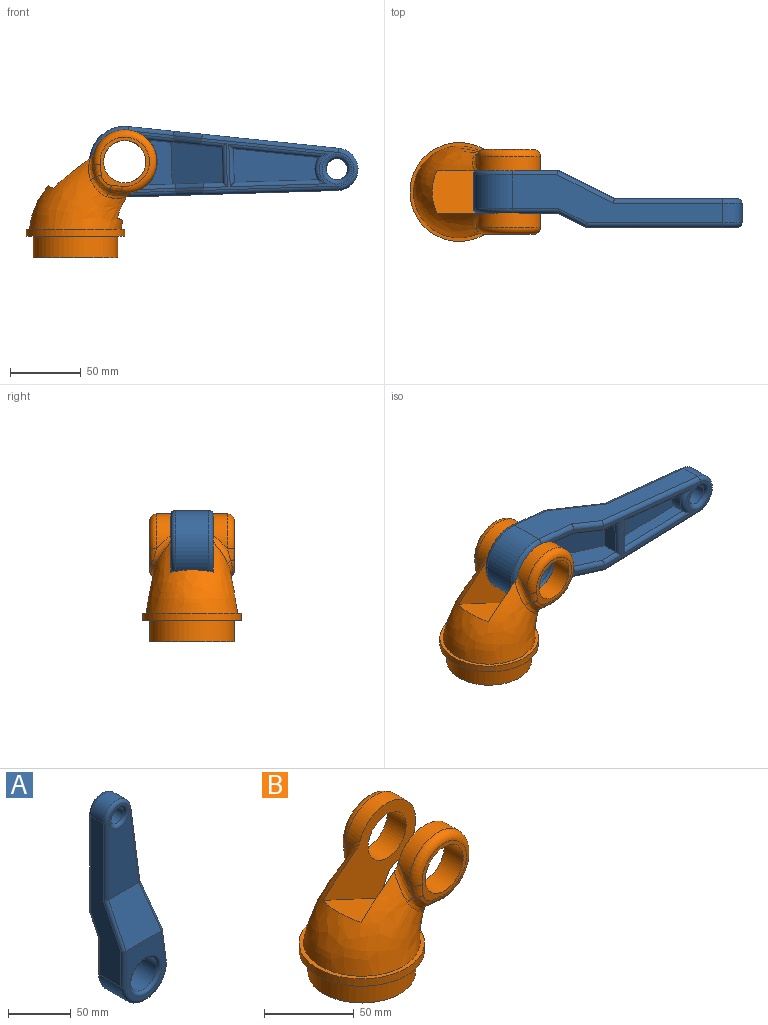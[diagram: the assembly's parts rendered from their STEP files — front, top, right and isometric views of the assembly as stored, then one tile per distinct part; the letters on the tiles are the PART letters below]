
ASSEMBLY  parts=2 mates=1
PART A: 56 faces, bbox 54.1x40x193.3 mm
  f0: plane 60.11x9mm, normal (-0.99,0,-0.13), area 545.8mm2, adj f19,f21,f22,f40
  f1: plane 53.62x29mm, normal (1,0,0), area 928.8mm2, adj f2,f16,f20,f23,f44,f45,f47
  f2: plane 36x29.72mm, normal (0,0.89,-0.45), area 1099.1mm2, adj f1,f16,f17,f23
  f3: plane 107.01x36.83mm, normal (0,1,0), area 546mm2, adj f5,f6,f24,f25,f27,f29,f40,f41
  f4: plane 57.02x44.01mm, normal (0,1,0), area 511.3mm2, adj f5,f6,f28,f29,f30,f31,f44,f46
  f5: plane 20.02x10.01mm, normal (0,0.89,-0.45), area 45.1mm2, adj f3,f4,f29,f48,f50,f51
  f6: plane 20x10mm, normal (0,0.89,-0.45), area 44.7mm2, adj f3,f4,f26,f45
  f7: plane 57x44mm, normal (0,-1,0), area 1207mm2, adj f13,f36,f38,f39,f53
  f8: cylinder r=25mm len=50mm, axis (0,1,0), area 1964.8mm2, adj f9,f11,f30,f38
  f9: plane 148.67x34mm, normal (0.99,0,0.13), area 2704.9mm2, adj f8,f10,f27,f29,f31,f35,f37,f39
  f10: cylinder r=15mm len=29.87mm, axis (0,1,0), area 631.8mm2, adj f9,f11,f25,f33
  f11: plane 150x34mm, normal (-1,0,0), area 2728.8mm2, adj f8,f10,f24,f26,f28,f32,f34,f36
  f12: plane 87x34.15mm, normal (0,-1,0), area 2064.6mm2, adj f13,f32,f33,f35,f52
  f13: plane 40.02x39.69mm, normal (0,-0.89,0.45), area 1655.1mm2, adj f7,f12,f34,f35,f37,f39
  f14: cylinder r=15mm len=30mm, axis (0,1,0), area 2261.9mm2, adj f53,f54
  f15: cylinder r=7.5mm len=15mm, axis (0,1,0), area 659.7mm2, adj f52,f55
  f16: plane 31.79x17.62mm, normal (0,1,0), area 369.9mm2, adj f1,f2,f17,f20
  f17: plane 51.5x29mm, normal (-0.99,0,-0.13), area 900.5mm2, adj f2,f16,f20,f23,f48,f50,f51
  f18: plane 59.06x9mm, normal (1,0,0), area 531.5mm2, adj f19,f21,f22,f43
  f19: plane 60.11x23.82mm, normal (0,1,0), area 1158.7mm2, adj f0,f18,f21,f22
  f20: cylinder r=23mm len=31.79mm, axis (0,1,0), area 668.8mm2, adj f1,f16,f17,f46
  f21: cylinder r=15.5mm len=15.77mm, axis (0,1,0), area 149.3mm2, adj f0,f18,f19,f42
  f22: plane 23.82x9mm, normal (0,0,1), area 214.4mm2, adj f0,f18,f19,f41
  f23: plane 24.9x11mm, normal (0,0,-1), area 273.9mm2, adj f1,f2,f17,f49
  f24: cylinder r=3mm len=95mm, axis (0,0,-1), area 446.5mm2, adj f3,f11,f25,f26
  f25: torus R=12mm, axis (0,-1,0), area 197.2mm2, adj f3,f10,f24,f27
  f26: cylinder r=3mm len=21.98mm, axis (0,-0.45,-0.89), area 105.4mm2, adj f6,f11,f24,f28
  f27: cylinder r=3mm len=96.98mm, axis (-0.13,0,0.99), area 458mm2, adj f3,f9,f25,f29
  f28: cylinder r=3mm len=35.71mm, axis (0,0,-1), area 166.1mm2, adj f4,f11,f26,f30
  f29: cylinder r=3mm len=22.37mm, axis (-0.12,0.44,0.89), area 110.1mm2, adj f3,f4,f5,f9,f27,f31
  f30: torus R=22mm, axis (0,-1,0), area 369mm2, adj f4,f8,f28,f31
  f31: cylinder r=3mm len=33.19mm, axis (-0.13,0,0.99), area 153.8mm2, adj f4,f9,f29,f30
  f32: cylinder r=3mm len=75.71mm, axis (0,0,1), area 354.6mm2, adj f11,f12,f33,f34
  f33: torus R=12mm, axis (0,1,0), area 197.2mm2, adj f10,f12,f32,f35
  f34: cylinder r=3mm len=41.98mm, axis (0,0.45,0.89), area 210.7mm2, adj f11,f13,f32,f36
  f35: cylinder r=3mm len=77.7mm, axis (0.13,0,-0.99), area 365.4mm2, adj f9,f12,f13,f33,f37
  f36: cylinder r=3mm len=35mm, axis (0,0,1), area 163.7mm2, adj f7,f11,f34,f38
  f37: cylinder r=3mm len=41.6mm, axis (0.12,-0.44,-0.89), area 204.2mm2, adj f9,f13,f35,f39
  f38: torus R=22mm, axis (0,-1,0), area 369mm2, adj f7,f8,f36,f39
  f39: cylinder r=3mm len=32.48mm, axis (0.13,0,-0.99), area 151.3mm2, adj f7,f9,f13,f37,f38
  f40: cylinder r=3mm len=70.18mm, axis (0.13,0,-0.99), area 301.3mm2, adj f0,f3,f41,f42
  f41: cylinder r=3mm len=30.25mm, axis (-1,0,0), area 123.3mm2, adj f3,f22,f40,f43
  f42: torus R=12.5mm, axis (0,-1,0), area 90.8mm2, adj f3,f21,f40,f43
  f43: cylinder r=3mm len=68.39mm, axis (0,0,1), area 293.1mm2, adj f3,f18,f41,f42
  f44: cylinder r=3mm len=35.71mm, axis (0,0,1), area 110.5mm2, adj f1,f4,f45,f46
  f45: cylinder r=3mm len=21.98mm, axis (0,0.45,0.89), area 105.4mm2, adj f1,f6,f44,f47
  f46: torus R=20mm, axis (0,-1,0), area 191.3mm2, adj f4,f20,f44,f48
  f47: cylinder r=3mm len=17.11mm, axis (0,0,1), area 70.4mm2, adj f1,f3,f45,f49
  f48: cylinder r=3mm len=33.45mm, axis (0.13,0,-0.99), area 99.4mm2, adj f4,f5,f17,f46,f50
  f49: cylinder r=3mm len=30.52mm, axis (1,0,0), area 127mm2, adj f3,f23,f47,f51
  f50: cylinder r=3mm len=21.6mm, axis (0.12,-0.44,-0.89), area 102.1mm2, adj f5,f17,f48,f51
  f51: cylinder r=3mm len=17.51mm, axis (0.13,0,-0.99), area 72.2mm2, adj f3,f5,f17,f49,f50
  f52: torus R=10.5mm, axis (0,1,0), area 254.3mm2, adj f12,f15
  f53: torus R=18mm, axis (0,-1,0), area 476.4mm2, adj f7,f14
  f54: torus R=18mm, axis (0,-1,0), area 476.4mm2, adj f4,f14
  f55: torus R=10.5mm, axis (0,-1,0), area 254.3mm2, adj f3,f15
PART B: 29 faces, bbox 95.6x71.2x93.5 mm
  f0: bspline ~81.29x65mm, area 5808.1mm2, adj f2,f3,f5,f11,f12,f13,f14,f24
  f1: cylinder r=22.5mm len=45mm, axis (0,1,0), area 1015.6mm2, adj f2,f3,f15,f24
  f2: bspline ~21.91x19.31mm, area 111.9mm2, adj f0,f1,f14,f17,f24
  f3: bspline ~24.51x21.07mm, area 112.3mm2, adj f0,f1,f14,f16,f24
  f4: cylinder r=15mm len=30mm, axis (0,-1,0), area 1413.7mm2, adj f10,f24
  f5: plane 70x70mm, normal (0,0,1), area 530.2mm2, adj f0,f6
  f6: cylinder r=35mm len=70mm, axis (0,0,-1), area 1099.6mm2, adj f5,f7
  f7: plane 70x70mm, normal (0,0,-1), area 1021mm2, adj f6,f28
  f8: cylinder r=22.5mm len=45mm, axis (0,1,0), area 1015.6mm2, adj f11,f13,f21,f25
  f9: plane 35x35mm, normal (0,-1,0), area 286.2mm2, adj f19,f20,f21,f22,f23
  f10: plane 35x35mm, normal (0,1,0), area 286.2mm2, adj f4,f15,f16,f17,f18
  f11: bspline ~24.51x21.07mm, area 112.3mm2, adj f0,f8,f12,f19,f25
  f12: bspline ~17.12x16.29mm, area 73.1mm2, adj f0,f11,f13,f20
  f13: bspline ~21.91x19.31mm, area 111.9mm2, adj f0,f8,f12,f22,f25
  f14: bspline ~17.68x16.44mm, area 73.1mm2, adj f0,f2,f3,f18
  f15: torus R=17.5mm, axis (0,-1,0), area 797.9mm2, adj f1,f10,f16,f17
  f16: bspline ~13.16x7.21mm, area 53.8mm2, adj f3,f10,f15,f18
  f17: bspline ~13.9x7.88mm, area 51.4mm2, adj f2,f10,f15,f18
  f18: bspline ~11.88x11.8mm, area 57mm2, adj f10,f14,f16,f17
  f19: bspline ~14.1x7.65mm, area 53.8mm2, adj f9,f11,f20,f21
  f20: bspline ~12.15x12.07mm, area 57mm2, adj f9,f12,f19,f22
  f21: torus R=17.5mm, axis (0,-1,0), area 797.9mm2, adj f8,f9,f19,f22
  f22: bspline ~12.67x6.97mm, area 51.4mm2, adj f9,f13,f20,f21
  f23: cylinder r=15mm len=30mm, axis (0,-1,0), area 1413.7mm2, adj f9,f25
  f24: plane 73.4x62.85mm, normal (0,-1,0), area 1806.7mm2, adj f0,f1,f2,f3,f4,f26
  f25: plane 73.4x62.85mm, normal (0,1,0), area 1806.7mm2, adj f0,f8,f11,f13,f23,f26
  f26: plane 54.18x31.24mm, normal (0.42,0,0.91), area 1671.4mm2, adj f0,f24,f25
  f27: plane 60x60mm, normal (0,0,-1), area 2827.4mm2, adj f28
  f28: cylinder r=30mm len=60mm, axis (0,0,1), area 2827.4mm2, adj f7,f27
PLACE A rot(axis=(-0.7,0,-0.72),180deg) t=(35,-25,52.89)mm
PLACE B at identity fixed
MATE revolute A.f8 <-> B.f1  axis (0,-1,0) through (35,0,52.89)mm
